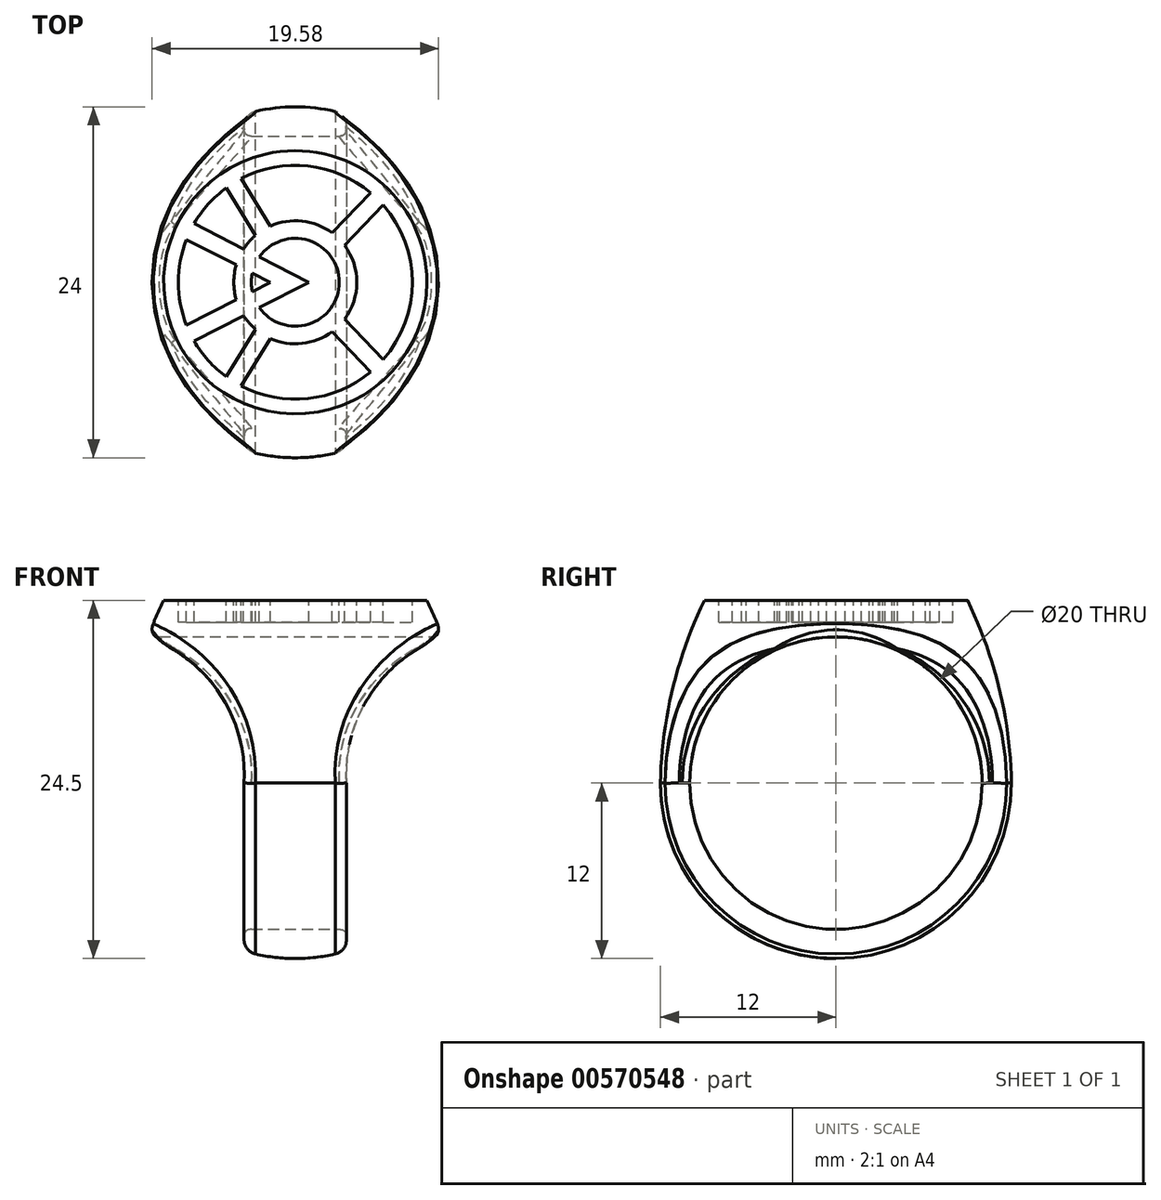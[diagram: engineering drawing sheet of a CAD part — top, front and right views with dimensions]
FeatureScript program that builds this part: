
annotation { "Feature Type Name" : "Feature", "Feature Type Description" : "" }
export const myFeature = defineFeature(function(context is Context, id is Id, definition is map)
    precondition{}
    {
        {
            var Q0;
            Q0=qCreatedBy(makeId("Right.planeOp"),FACE);
            var sketch = newSketch(context, id + "F0", { "sketchPlane" : qUnion([Q0])});
            skLineSegment(sketch, "E0", {"start": v(0, 0) * mm, "end": v(0, -24.5) * mm});
            skLineSegment(sketch, "E1", {"start": v(0, 0) * mm, "end": v(-9, 0) * mm});
            skArc(sketch, "E2", {"start": v(-12, -12.5) * mm, "mid": v(-8.49, -20.99) * mm, "end": v(0, -24.5) * mm});
            skLineSegment(sketch, "E3", {"start": v(0, -12.5) * mm, "end": v(-12, -12.5) * mm, "construction": true});
            skArc(sketch, "E4", {"start": v(-9, 0) * mm, "mid": v(-11.18, -6.09) * mm, "end": v(-12, -12.5) * mm});
            skSolve(sketch);
        }
        {
            var Q0;
            Q0=makeQuery(id+"F0.imprint","IMPRINT",FACE,{"disambiguationData":[TD([[makeQuery(id+"F0.imprint","IMPRINT",EDGE,{"derivedFrom":sQuery(id+"F0.wireOp",EDGE,"E0")}),-1.0]])]});
            var Q1;
            Q1=sQuery(id+"F0.wireOp",EDGE,"E0");
            revolve(context, id + "F1", {"entities" : qUnion([Q0]), "axis" : qUnion([Q1]), "revolveType" : RevolveType.FULL});
        }
        {
            var Q0;
            Q0=qCreatedBy(makeId("Right.planeOp"),FACE);
            var sketch = newSketch(context, id + "F2", { "sketchPlane" : qUnion([Q0])});
            skCircle(sketch, "E5", {"center": v(0, -12.5) * mm, "radius": 10 * mm});
            skSolve(sketch);
        }
        {
            var Q0;
            Q0=qSketchRegion(id+"F2",true);
            extrude(context, id + "F3", {"entities" : qUnion([Q0]), "operationType" : NewBodyOperationType.REMOVE, "oppositeDirection" : true, "depth" : 25 * mm, "offsetDistance" : 25 * mm, "symmetric" : true});
        }
        {
            var Q0;
            Q0=qCreatedBy(makeId("Front.planeOp"),FACE);
            var sketch = newSketch(context, id + "F4", { "sketchPlane" : qUnion([Q0])});
            skLineSegment(sketch, "E6", {"start": v(3.5, -26.5) * mm, "end": v(3.5, -12.5) * mm});
            skArc(sketch, "E7", {"start": v(10.15, -2.5) * mm, "mid": v(5.16, -6.39) * mm, "end": v(3.5, -12.5) * mm});
            skLineSegment(sketch, "E8", {"start": v(10.15, -2.5) * mm, "end": v(11.65, -2.5) * mm});
            skLineSegment(sketch, "E9", {"start": v(11.65, -2.5) * mm, "end": v(11.65, -26.5) * mm});
            skLineSegment(sketch, "E10", {"start": v(11.65, -26.5) * mm, "end": v(3.5, -26.5) * mm});
            skPoint(sketch, "E11.start.orphan", {"position": v(0, -24.5) * mm});
            skLineSegment(sketch, "E12", {"start": v(0, 0) * mm, "end": v(0, -24.5) * mm, "construction": true});
            skLineSegment(sketch, "E13.MirrorCS", {"start": v(-3.5, -26.5) * mm, "end": v(-3.5, -12.5) * mm});
            skArc(sketch, "E14.MirrorCS", {"start": v(-10.15, -2.5) * mm, "mid": v(-5.16, -6.39) * mm, "end": v(-3.5, -12.5) * mm});
            skLineSegment(sketch, "E15.MirrorCS", {"start": v(-11.65, -2.5) * mm, "end": v(-11.65, -26.5) * mm});
            skLineSegment(sketch, "E16.MirrorCS", {"start": v(-11.65, -26.5) * mm, "end": v(-3.5, -26.5) * mm});
            skLineSegment(sketch, "E17.MirrorCS", {"start": v(-10.15, -2.5) * mm, "end": v(-11.65, -2.5) * mm});
            skSolve(sketch);
        }
        {
            var Q0;
            Q0=qSketchRegion(id+"F4",true);
            extrude(context, id + "F5", {"entities" : qUnion([Q0]), "operationType" : NewBodyOperationType.REMOVE, "depth" : 25 * mm, "offsetDistance" : 25 * mm, "symmetric" : true});
        }
        {
            var Q0;
            Q0=makeQuery(id+"F1.opRevolve","SWEPT_FACE",FACE,{"disambiguationData":[OSD([sQuery(id+"F0.wireOp",EDGE,"E1")])]});
            var sketch = newSketch(context, id + "F6", { "sketchPlane" : qUnion([Q0])});
            skArc(sketch, "E18", {"start": v(-7.45, 2.93) * mm, "mid": v(-8, 0) * mm, "end": v(-7.45, -2.93) * mm});
            skLineSegment(sketch, "E19", {"start": v(-8, 0) * mm, "end": v(8, 0) * mm, "construction": true});
            skArc(sketch, "E20", {"start": v(3, 0) * mm, "mid": v(0.9, 2.87) * mm, "end": v(-2.46, 1.73) * mm});
            skArc(sketch, "E21", {"start": v(4.2, 0) * mm, "mid": v(4, 1.33) * mm, "end": v(3.36, 2.53) * mm});
            skLineSegment(sketch, "E22", {"start": v(0.94, 0) * mm, "end": v(-2.46, 1.73) * mm});
            skLineSegment(sketch, "E23", {"start": v(-7.45, 2.93) * mm, "end": v(-4.04, 1.19) * mm});
            skLineSegment(sketch, "E24", {"start": v(-4.72, 6.46) * mm, "end": v(-2.72, 3.2) * mm});
            skLineSegment(sketch, "E25", {"start": v(-3.7, 7.09) * mm, "end": v(-1.7, 3.85) * mm});
            skLineSegment(sketch, "E26", {"start": v(5.15, 6.12) * mm, "end": v(2.51, 3.37) * mm});
            skLineSegment(sketch, "E27", {"start": v(6, 5.28) * mm, "end": v(3.36, 2.53) * mm});
            skArc(sketch, "E28.trimOffspring", {"start": v(-4.04, 1.19) * mm, "mid": v(-4.16, 0.6) * mm, "end": v(-4.2, 0) * mm});
            skArc(sketch, "E29.trimOffspring", {"start": v(-2.94, 0.63) * mm, "mid": v(-2.99, 0.32) * mm, "end": v(-3, 0) * mm});
            skLineSegment(sketch, "E30.trimOffspring", {"start": v(-3.53, 2.28) * mm, "end": v(-6.92, 4) * mm});
            skLineSegment(sketch, "E31.trimOffspring", {"start": v(-2.94, 0.63) * mm, "end": v(-1.7, 0) * mm});
            skArc(sketch, "E32.trimOffspring", {"start": v(-2.72, 3.2) * mm, "mid": v(-3.16, 2.77) * mm, "end": v(-3.53, 2.28) * mm});
            skArc(sketch, "E33.trimOffspring", {"start": v(-4.72, 6.46) * mm, "mid": v(-5.95, 5.35) * mm, "end": v(-6.92, 4) * mm});
            skArc(sketch, "E34.trimOffspring", {"start": v(5.15, 6.12) * mm, "mid": v(0.87, 7.95) * mm, "end": v(-3.7, 7.09) * mm});
            skArc(sketch, "E35.trimOffspring", {"start": v(2.51, 3.37) * mm, "mid": v(0.47, 4.18) * mm, "end": v(-1.7, 3.85) * mm});
            skLineSegment(sketch, "E36.MirrorCS", {"start": v(-7.45, -2.93) * mm, "end": v(-4.04, -1.19) * mm});
            skLineSegment(sketch, "E37.MirrorCS", {"start": v(-3.53, -2.28) * mm, "end": v(-6.92, -4) * mm});
            skArc(sketch, "E38.MirrorCS", {"start": v(-4.04, -1.19) * mm, "mid": v(-4.16, -0.6) * mm, "end": v(-4.2, 0) * mm});
            skLineSegment(sketch, "E39.MirrorCS", {"start": v(-2.94, -0.63) * mm, "end": v(-1.7, 0) * mm});
            skArc(sketch, "E40.MirrorCS", {"start": v(-2.94, -0.63) * mm, "mid": v(-2.99, -0.32) * mm, "end": v(-3, 0) * mm});
            skLineSegment(sketch, "E41.MirrorCS", {"start": v(0.94, 0) * mm, "end": v(-2.46, -1.73) * mm});
            skArc(sketch, "E42.MirrorCS", {"start": v(3, 0) * mm, "mid": v(0.9, -2.87) * mm, "end": v(-2.46, -1.73) * mm});
            skArc(sketch, "E43.MirrorCS", {"start": v(-2.72, -3.2) * mm, "mid": v(-3.16, -2.77) * mm, "end": v(-3.53, -2.28) * mm});
            skLineSegment(sketch, "E44.MirrorCS", {"start": v(-4.72, -6.46) * mm, "end": v(-2.72, -3.2) * mm});
            skLineSegment(sketch, "E45.MirrorCS", {"start": v(-3.7, -7.09) * mm, "end": v(-1.7, -3.85) * mm});
            skArc(sketch, "E46.MirrorCS", {"start": v(2.51, -3.37) * mm, "mid": v(0.47, -4.18) * mm, "end": v(-1.7, -3.85) * mm});
            skLineSegment(sketch, "E47.MirrorCS", {"start": v(5.15, -6.12) * mm, "end": v(2.51, -3.37) * mm});
            skLineSegment(sketch, "E48.MirrorCS", {"start": v(6, -5.28) * mm, "end": v(3.36, -2.53) * mm});
            skArc(sketch, "E49.MirrorCS", {"start": v(4.2, 0) * mm, "mid": v(4, -1.33) * mm, "end": v(3.36, -2.53) * mm});
            skArc(sketch, "E50.trimOffspring", {"start": v(-6.92, -4) * mm, "mid": v(-5.95, -5.35) * mm, "end": v(-4.72, -6.46) * mm});
            skArc(sketch, "E51.trimOffspring", {"start": v(-3.7, -7.09) * mm, "mid": v(0.87, -7.95) * mm, "end": v(5.15, -6.12) * mm});
            skArc(sketch, "E52.trimOffspring", {"start": v(6, -5.28) * mm, "mid": v(8, 0) * mm, "end": v(6, 5.28) * mm});
            skSolve(sketch);
        }
        {
            var Q0;
            Q0=qSketchRegion(id+"F6",true);
            var Q1;
            Q1=makeQuery(id+"F6.imprint","IMPRINT",FACE,{"disambiguationData":[TD([[makeQuery(id+"F6.imprint","IMPRINT",EDGE,{"derivedFrom":sQuery(id+"F6.wireOp",EDGE,"g20j87Mm-wGr7-AMiz-bI8b-qS7GuHKO57cL")}),1.0]])]});
            extrude(context, id + "F7", {"entities" : qUnion([Q0, Q1]), "operationType" : NewBodyOperationType.REMOVE, "oppositeDirection" : true, "depth" : 1.5 * mm, "offsetDistance" : 25 * mm});
        }
        {
            var Q0;
            Q0=makeQuery(id+"F5.boolean.opBoolean","INTERSECT",EDGE,{"disambiguationData":[OD(1.0)],"derivedFrom":[makeQuery(id+"F1.opRevolve","SWEPT_FACE",FACE,{"disambiguationData":[OSD([sQuery(id+"F0.wireOp",EDGE,"E4")])]}),makeQuery(id+"F5.opExtrude","SWEPT_FACE",FACE,{"disambiguationData":[OSD([sQuery(id+"F4.wireOp",EDGE,"E14.MirrorCS")])]})]});
            var Q1;
            Q1=makeQuery(id+"F5.boolean.opBoolean","INTERSECT",EDGE,{"derivedFrom":[makeQuery(id+"F1.opRevolve","SWEPT_FACE",FACE,{"disambiguationData":[OSD([sQuery(id+"F0.wireOp",EDGE,"E2")])]}),makeQuery(id+"F5.opExtrude","SWEPT_FACE",FACE,{"disambiguationData":[OSD([sQuery(id+"F4.wireOp",EDGE,"E13.MirrorCS")])]})]});
            var Q2;
            Q2=makeQuery(id+"F5.boolean.opBoolean","INTERSECT",EDGE,{"disambiguationData":[OD(1.0)],"derivedFrom":[makeQuery(id+"F1.opRevolve","SWEPT_FACE",FACE,{"disambiguationData":[OSD([sQuery(id+"F0.wireOp",EDGE,"E4")])]}),makeQuery(id+"F5.opExtrude","SWEPT_FACE",FACE,{"disambiguationData":[OSD([sQuery(id+"F4.wireOp",EDGE,"E7")])]})]});
            var Q3;
            Q3=makeQuery(id+"F5.boolean.opBoolean","INTERSECT",EDGE,{"derivedFrom":[makeQuery(id+"F1.opRevolve","SWEPT_FACE",FACE,{"disambiguationData":[OSD([sQuery(id+"F0.wireOp",EDGE,"E2")])]}),makeQuery(id+"F5.opExtrude","SWEPT_FACE",FACE,{"disambiguationData":[OSD([sQuery(id+"F4.wireOp",EDGE,"E6")])]})]});
            fillet(context, id + "F8", {"entities" : qUnion([Q0, Q1, Q2, Q3]), "radius" : 1 * mm, "allowEdgeOverflow" : false});
        }
        {
            var Q0;
            Q0=makeQuery(id+"F5.boolean.opBoolean","INTERSECT",EDGE,{"disambiguationData":[OD(1.0)],"derivedFrom":[makeQuery(id+"F3.boolean.opBoolean","COPY",FACE,{"derivedFrom":makeQuery(id+"F3.opExtrude","SWEPT_FACE",FACE,{"disambiguationData":[OSD([sQuery(id+"F2.wireOp",EDGE,"E5")])]})}),makeQuery(id+"F5.opExtrude","SWEPT_FACE",FACE,{"disambiguationData":[OSD([sQuery(id+"F4.wireOp",EDGE,"E14.MirrorCS")])]})]});
            var Q1;
            Q1=makeQuery(id+"F5.boolean.opBoolean","INTERSECT",EDGE,{"derivedFrom":[makeQuery(id+"F3.boolean.opBoolean","COPY",FACE,{"derivedFrom":makeQuery(id+"F3.opExtrude","SWEPT_FACE",FACE,{"disambiguationData":[OSD([sQuery(id+"F2.wireOp",EDGE,"E5")])]})}),makeQuery(id+"F5.opExtrude","SWEPT_FACE",FACE,{"disambiguationData":[OSD([sQuery(id+"F4.wireOp",EDGE,"E13.MirrorCS")])]})]});
            var Q2;
            Q2=makeQuery(id+"F5.boolean.opBoolean","INTERSECT",EDGE,{"disambiguationData":[OD(0.0)],"derivedFrom":[makeQuery(id+"F3.boolean.opBoolean","COPY",FACE,{"derivedFrom":makeQuery(id+"F3.opExtrude","SWEPT_FACE",FACE,{"disambiguationData":[OSD([sQuery(id+"F2.wireOp",EDGE,"E5")])]})}),makeQuery(id+"F5.opExtrude","SWEPT_FACE",FACE,{"disambiguationData":[OSD([sQuery(id+"F4.wireOp",EDGE,"E14.MirrorCS")])]})]});
            var Q3;
            Q3=makeQuery(id+"F5.boolean.opBoolean","INTERSECT",EDGE,{"disambiguationData":[OD(0.0)],"derivedFrom":[makeQuery(id+"F3.boolean.opBoolean","COPY",FACE,{"derivedFrom":makeQuery(id+"F3.opExtrude","SWEPT_FACE",FACE,{"disambiguationData":[OSD([sQuery(id+"F2.wireOp",EDGE,"E5")])]})}),makeQuery(id+"F5.opExtrude","SWEPT_FACE",FACE,{"disambiguationData":[OSD([sQuery(id+"F4.wireOp",EDGE,"E7")])]})]});
            var Q4;
            Q4=makeQuery(id+"F3.boolean.opBoolean","COPY",FACE,{"derivedFrom":makeQuery(id+"F3.opExtrude","SWEPT_FACE",FACE,{"disambiguationData":[OSD([sQuery(id+"F2.wireOp",EDGE,"E5")])]})});
            fillet(context, id + "F9", {"entities" : qUnion([Q0, Q1, Q2, Q3, Q4]), "radius" : .5 * mm, "rho" : 0.5, "crossSection" : FilletCrossSection.CONIC, "allowEdgeOverflow" : false});
        }
    });
